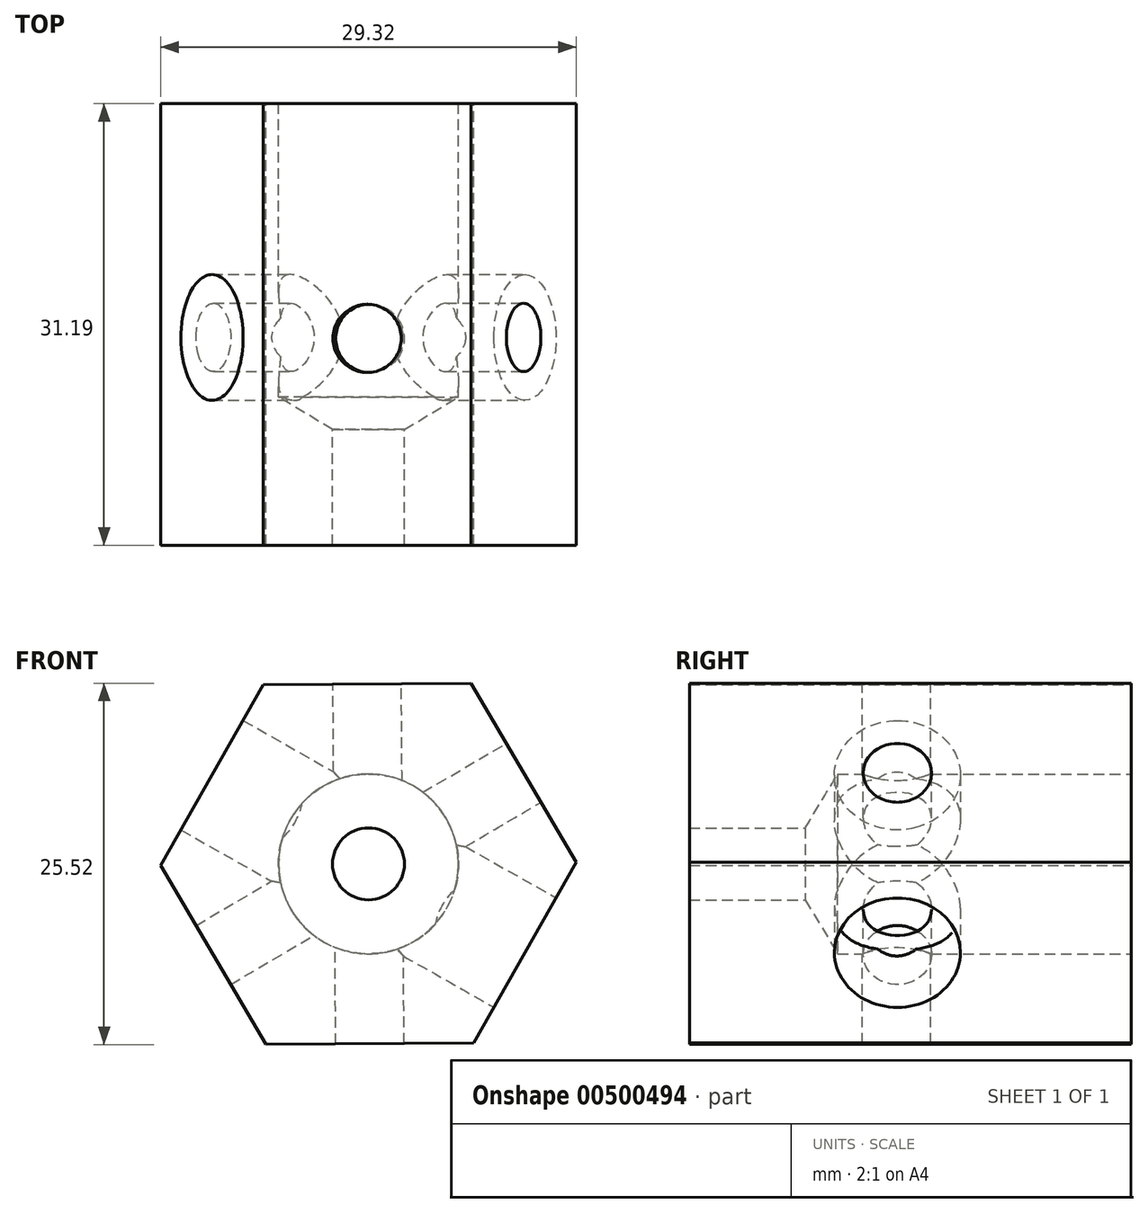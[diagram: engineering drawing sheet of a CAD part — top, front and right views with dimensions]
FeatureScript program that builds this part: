
annotation { "Feature Type Name" : "Feature", "Feature Type Description" : "" }
export const myFeature = defineFeature(function(context is Context, id is Id, definition is map)
    precondition{}
    {
        {
            var Q0;
            Q0=qCreatedBy(makeId("Front.planeOp"),FACE);
            var sketch = newSketch(context, id + "F0", { "sketchPlane" : qUnion([Q0])});
            skCircle(sketch, "E0.cCircle", {"center": v(0, 0) * mm, "radius": 12.7 * mm, "construction": true});
            skLineSegment(sketch, "E0.0", {"start": v(-7.24, -12.76) * mm, "end": v(-14.66, -0.11) * mm});
            skLineSegment(sketch, "E0.1", {"start": v(-14.66, -0.11) * mm, "end": v(-7.43, 12.64) * mm});
            skLineSegment(sketch, "E0.2", {"start": v(-7.43, 12.64) * mm, "end": v(7.24, 12.76) * mm});
            skLineSegment(sketch, "E0.3", {"start": v(7.24, 12.76) * mm, "end": v(14.66, 0.11) * mm});
            skLineSegment(sketch, "E0.4", {"start": v(14.66, 0.11) * mm, "end": v(7.43, -12.64) * mm});
            skLineSegment(sketch, "E0.5", {"start": v(7.43, -12.64) * mm, "end": v(-7.24, -12.76) * mm});
            skPoint(sketch, "E0.0.midPoint", {"position": v(-10.95, -6.43) * mm});
            skSolve(sketch);
        }
        {
            var Q0;
            Q0 = qSketchRegion(id + "F0", true);
            extrude(context, id + "F1", {"entities" : qUnion([Q0]), "depth" : 31.2 * mm});
        }
        {
            var Q0;
            Q0=sQuery(id+"F0.wireOp",VERTEX,"E0.cCircle.center");
            var Q1;
            Q1=makeQuery(id+"F1.opExtrude","SWEPT_BODY",BODY,{"disambiguationData":[OSD([sQuery(id+"F0.wireOp",EDGE,"E0.0"),sQuery(id+"F0.wireOp",EDGE,"E0.1"),sQuery(id+"F0.wireOp",EDGE,"E0.2"),sQuery(id+"F0.wireOp",EDGE,"E0.3"),sQuery(id+"F0.wireOp",EDGE,"E0.4"),sQuery(id+"F0.wireOp",EDGE,"E0.5")])]});
            hole(context, id + "F2", {"style" : HoleStyle.SIMPLE, "endStyle" : HoleEndStyle.BLIND, "oppositeDirection" : true, "holeDiameter" : 12.7 * mm, "holeDepth" : 20.73 * mm, "isTappedThrough" : true, "tappedDepth" : 12.7 * mm, "tapClearance" : 3, "locations" : qUnion([Q0]), "scope" : qUnion([Q1])});
        }
        {
            var Q0;
            Q0=sQuery(id+"F0.wireOp",VERTEX,"E0.cCircle.center");
            var Q1;
            Q1=makeQuery(id+"F1.opExtrude","SWEPT_BODY",BODY,{"disambiguationData":[OSD([sQuery(id+"F0.wireOp",EDGE,"E0.0"),sQuery(id+"F0.wireOp",EDGE,"E0.1"),sQuery(id+"F0.wireOp",EDGE,"E0.2"),sQuery(id+"F0.wireOp",EDGE,"E0.3"),sQuery(id+"F0.wireOp",EDGE,"E0.4"),sQuery(id+"F0.wireOp",EDGE,"E0.5")])]});
            hole(context, id + "F3", {"style" : HoleStyle.SIMPLE, "endStyle" : HoleEndStyle.THROUGH, "oppositeDirection" : true, "holeDiameter" : 5.08 * mm, "isTappedThrough" : true, "tappedDepth" : 12.7 * mm, "tapClearance" : 3, "locations" : qUnion([Q0]), "scope" : qUnion([Q1])});
        }
        {
            var Q0;
            Q0=makeQuery(id+"F1.opExtrude","SWEPT_FACE",FACE,{"disambiguationData":[OSD([sQuery(id+"F0.wireOp",EDGE,"E0.3")])]});
            var sketch = newSketch(context, id + "F4", { "sketchPlane" : qUnion([Q0])});
            skLineSegment(sketch, "E1", {"start": v(0, 0) * mm, "end": v(-16.51, 0) * mm});
            skPoint(sketch, "E1.endSnap0", {"position": v(0, 0) * mm});
            skPoint(sketch, "E2", {"position": v(-16.51, 0) * mm});
            skPoint(sketch, "E3", {"position": v(20.22, 35.28) * mm});
            skSolve(sketch);
        }
        {
            var Q0;
            Q0=sQuery(id+"F4.wireOp",VERTEX,"E2");
            var Q1;
            Q1=makeQuery(id+"F1.opExtrude","SWEPT_BODY",BODY,{"disambiguationData":[OSD([sQuery(id+"F0.wireOp",EDGE,"E0.0"),sQuery(id+"F0.wireOp",EDGE,"E0.1"),sQuery(id+"F0.wireOp",EDGE,"E0.2"),sQuery(id+"F0.wireOp",EDGE,"E0.3"),sQuery(id+"F0.wireOp",EDGE,"E0.4"),sQuery(id+"F0.wireOp",EDGE,"E0.5")])]});
            hole(context, id + "F5", {"style" : HoleStyle.SIMPLE, "endStyle" : HoleEndStyle.THROUGH, "holeDiameter" : 4.83 * mm, "isTappedThrough" : true, "tappedDepth" : 12.7 * mm, "tapClearance" : 3, "locations" : qUnion([Q0]), "scope" : qUnion([Q1])});
        }
        {
            var Q0;
            Q0=makeQuery(id+"F1.opExtrude","SWEPT_FACE",FACE,{"disambiguationData":[OSD([sQuery(id+"F0.wireOp",EDGE,"E0.2")])]});
            var sketch = newSketch(context, id + "F6", { "sketchPlane" : qUnion([Q0])});
            skLineSegment(sketch, "E4", {"start": v(0, 0) * mm, "end": v(0, -16.58) * mm});
            skPoint(sketch, "E5", {"position": v(0, -16.58) * mm});
            skSolve(sketch);
        }
        {
            var Q0;
            Q0=sQuery(id+"F6.wireOp",VERTEX,"E5");
            var Q1;
            Q1=makeQuery(id+"F1.opExtrude","SWEPT_BODY",BODY,{"disambiguationData":[OSD([sQuery(id+"F0.wireOp",EDGE,"E0.0"),sQuery(id+"F0.wireOp",EDGE,"E0.1"),sQuery(id+"F0.wireOp",EDGE,"E0.2"),sQuery(id+"F0.wireOp",EDGE,"E0.3"),sQuery(id+"F0.wireOp",EDGE,"E0.4"),sQuery(id+"F0.wireOp",EDGE,"E0.5")])]});
            hole(context, id + "F7", {"style" : HoleStyle.SIMPLE, "endStyle" : HoleEndStyle.THROUGH, "holeDiameter" : 4.83 * mm, "isTappedThrough" : true, "tappedDepth" : 12.7 * mm, "tapClearance" : 3, "locations" : qUnion([Q0]), "scope" : qUnion([Q1])});
        }
        {
            var Q0;
            Q0=makeQuery(id+"F1.opExtrude","SWEPT_FACE",FACE,{"disambiguationData":[OSD([sQuery(id+"F0.wireOp",EDGE,"E0.4")])]});
            var sketch = newSketch(context, id + "F8", { "sketchPlane" : qUnion([Q0])});
            skLineSegment(sketch, "E6", {"start": v(0, 0) * mm, "end": v(-16.51, 0) * mm});
            skPoint(sketch, "E6.endSnap0", {"position": v(0, 0) * mm});
            skSolve(sketch);
        }
        {
            var Q0;
            Q0=sQuery(id+"F8.wireOp",VERTEX,"E6.end");
            var Q1;
            Q1=makeQuery(id+"F1.opExtrude","SWEPT_BODY",BODY,{"disambiguationData":[OSD([sQuery(id+"F0.wireOp",EDGE,"E0.0"),sQuery(id+"F0.wireOp",EDGE,"E0.1"),sQuery(id+"F0.wireOp",EDGE,"E0.2"),sQuery(id+"F0.wireOp",EDGE,"E0.3"),sQuery(id+"F0.wireOp",EDGE,"E0.4"),sQuery(id+"F0.wireOp",EDGE,"E0.5")])]});
            hole(context, id + "F9", {"style" : HoleStyle.SIMPLE, "endStyle" : HoleEndStyle.THROUGH, "holeDiameter" : 8.9 * mm, "isTappedThrough" : true, "tappedDepth" : 12.7 * mm, "tapClearance" : 3, "locations" : qUnion([Q0]), "scope" : qUnion([Q1])});
        }
    });
